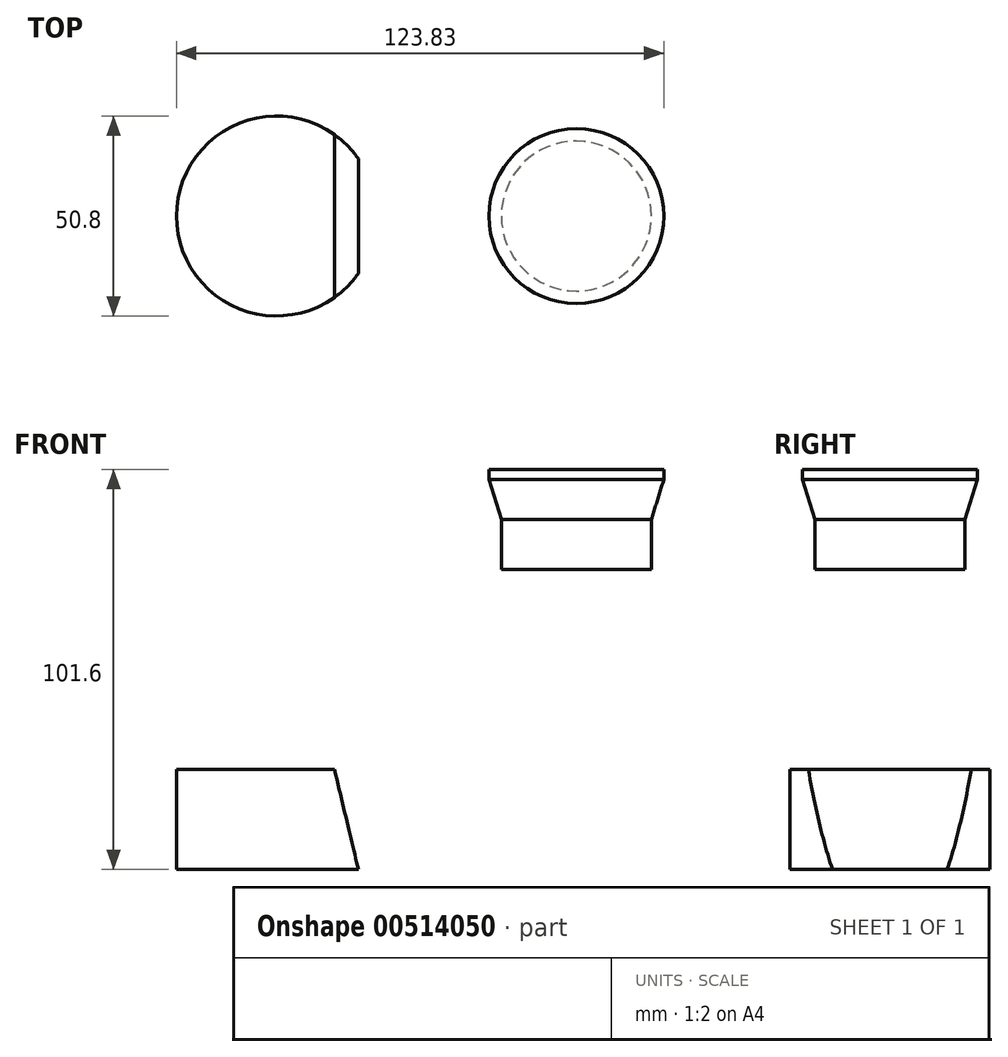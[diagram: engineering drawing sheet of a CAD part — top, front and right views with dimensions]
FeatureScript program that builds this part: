
annotation { "Feature Type Name" : "Feature", "Feature Type Description" : "" }
export const myFeature = defineFeature(function(context is Context, id is Id, definition is map)
    precondition{}
    {
        {
            var Q0;
            Q0=qCreatedBy(makeId("Top.planeOp"),FACE);
            var sketch = newSketch(context, id + "F0", { "sketchPlane" : qUnion([Q0])});
            skCircle(sketch, "E0", {"center": v(0, 0) * mm, "radius": 25.4 * mm});
            skSolve(sketch);
        }
        {
            var Q0;
            Q0=qSketchRegion(id+"F0",true);
            extrude(context, id + "F1", {"entities" : qUnion([Q0]), "depth" : 12.7 * mm, "hasSecondDirection" : true, "secondDirectionOppositeDirection" : true, "secondDirectionDepth" : 12.7 * mm});
        }
        {
            var Q0;
            Q0=qCreatedBy(makeId("Top.planeOp"),FACE);
            cPlane(context, id + "F2", {"entities" : qUnion([Q0]), "cplaneType" : CPlaneType.OFFSET, "offset" : 76.2 * mm, "width" : 152.4 * mm, "height" : 152.4 * mm});
        }
        {
            var Q0;
            Q0=qCreatedBy(id+"F2.planeOp",FACE);
            var sketch = newSketch(context, id + "F3", { "sketchPlane" : qUnion([Q0])});
            skCircle(sketch, "E1", {"center": v(76.2, 0) * mm, "radius": 19.05 * mm});
            skSolve(sketch);
        }
        {
            var Q0;
            Q0=qSketchRegion(id+"F3",true);
            extrude(context, id + "F4", {"entities" : qUnion([Q0]), "oppositeDirection" : true, "depth" : 12.7 * mm});
        }
        {
            var Q0;
            Q0=makeQuery(id+"F4.opExtrude","CAP_FACE",FACE,{"disambiguationData":[OSD([sQuery(id+"F3.wireOp",EDGE,"E1")])],"isStart":true});
            cPlane(context, id + "F5", {"entities" : qUnion([Q0]), "cplaneType" : CPlaneType.OFFSET, "offset" : 12.7 * mm, "width" : 152.4 * mm, "height" : 152.4 * mm});
        }
        {
            var Q0;
            Q0=qCreatedBy(id+"F5.planeOp",FACE);
            var sketch = newSketch(context, id + "F6", { "sketchPlane" : qUnion([Q0])});
            skCircle(sketch, "E2", {"center": v(76.2, 0) * mm, "radius": 22.22 * mm});
            skSolve(sketch);
        }
        {
            var Q0;
            Q0=qSketchRegion(id+"F6",true);
            extrude(context, id + "F7", {"entities" : qUnion([Q0]), "oppositeDirection" : true, "depth" : 2.54 * mm});
        }
        {
            var Q0;
            Q0=makeQuery(id+"F4.opExtrude","CAP_FACE",FACE,{"disambiguationData":[OSD([sQuery(id+"F3.wireOp",EDGE,"E1")])],"isStart":true});
            var Q1;
            Q1=makeQuery(id+"F7.opExtrude","CAP_FACE",FACE,{"disambiguationData":[OSD([sQuery(id+"F6.wireOp",EDGE,"E2")])],"isStart":false});
            loft(context, id + "F8", {"sheetProfilesArray" : [{ "sheetProfileEntities" : qUnion([Q0]) }, { "sheetProfileEntities" : qUnion([Q1]) }]});
        }
        {
            var Q0;
            Q0=qCreatedBy(makeId("Front.planeOp"),FACE);
            var sketch = newSketch(context, id + "F9", { "sketchPlane" : qUnion([Q0])});
            skLineSegment(sketch, "E3", {"start": v(11.6, 25.92) * mm, "end": v(22.05, -17.9) * mm});
            skPoint(sketch, "E4", {"position": v(17.78, 0) * mm});
            skArc(sketch, "E5", {"start": v(22.05, -17.9) * mm, "mid": v(27.62, 6.59) * mm, "end": v(11.6, 25.92) * mm});
            skArc(sketch, "E6", {"start": v(11.6, 25.92) * mm, "mid": v(-27.62, -6.59) * mm, "end": v(22.05, -17.9) * mm, "construction": true});
            skLineSegment(sketch, "E7", {"start": v(0, 0) * mm, "end": v(0, 12.7) * mm, "construction": true});
            skLineSegment(sketch, "E8", {"start": v(0, 12.7) * mm, "end": v(25.4, 12.7) * mm, "construction": true});
            skSolve(sketch);
        }
        {
            var Q0;
            Q0 = qSketchRegion(id + "F9", true);
            extrude(context, id + "F10", {"entities" : qUnion([Q0]), "operationType" : NewBodyOperationType.REMOVE, "oppositeDirection" : true, "depth" : 25.4 * mm, "hasSecondDirection" : true, "secondDirectionOppositeDirection" : false, "secondDirectionDepth" : 25.4 * mm});
        }
    });
